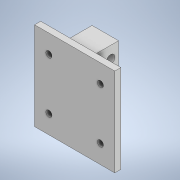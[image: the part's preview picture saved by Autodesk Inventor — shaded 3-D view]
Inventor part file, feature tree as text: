
AUTODESK INVENTOR PART (.ipt)
format: ipt  version: 2022 (Build 260153000, 153)  size: 158,720 bytes
history: native  units: in
note: dims shown in document units (in); Inventor stores cm internally (conversion verified against a paired STEP export)
features: reference x10, extrude x4, sketch x4, other x3
ambient origin geometry x8: Origin, YZ Plane, XZ Plane, XY Plane, X Axis, Y Axis, Z Axis, Center Point
bodies: Solid1 (feature_tree)
feature tree (21):
  extrude  "Extrusion1"  Depth=0.315in
  extrude  "Extrusion2"  Depth=0.5906in
  extrude  "Extrusion3"  Depth=0.7874in
  extrude  "Extrusion5"  Depth=0.3937in
  sketch  "Sketch1"  dims[d0=0.315in d1=0.315in]
  reference  "Reference1"
  reference  "Reference2"
  reference  "Reference3"
  reference  "Reference4"
  sketch  "Sketch2"  dims[d2=0.5906in d3=0.5906in]
  reference  "Reference5"
  reference  "Reference6"
  reference  "Reference7"
  reference  "Reference8"
  sketch  "Sketch3"  dims[d4=0.1969in d5=0.0in d6=0.7874in]
  sketch  "Sketch4"  dims[d7=0.7874in d8=0.3937in d9=0.3937in d10=0.7874in d11=0.0in d12=0.1969in d13=0.1969in d14=0.1969in d15=0.1969in d16=1.6535in d17=1.6535in d18=0.5906in d19=0.5906in d20=0.0in d21=0.0in d24=0.2756in d25=0.2756in d26=0.3937in d27=0.3937in d28=0.0in d29=0.0in]
  reference  "Reference11"
  reference  "Reference12"
  parser-record x1  (decoder bookkeeping rows leaked as tree rows — omitted from the tree; the rows remain in map.json)
  other  "model.iam"
  other  "base_link:1"
note: 1 file-system path scrubbed to <path> (originals preserved in map.json)
